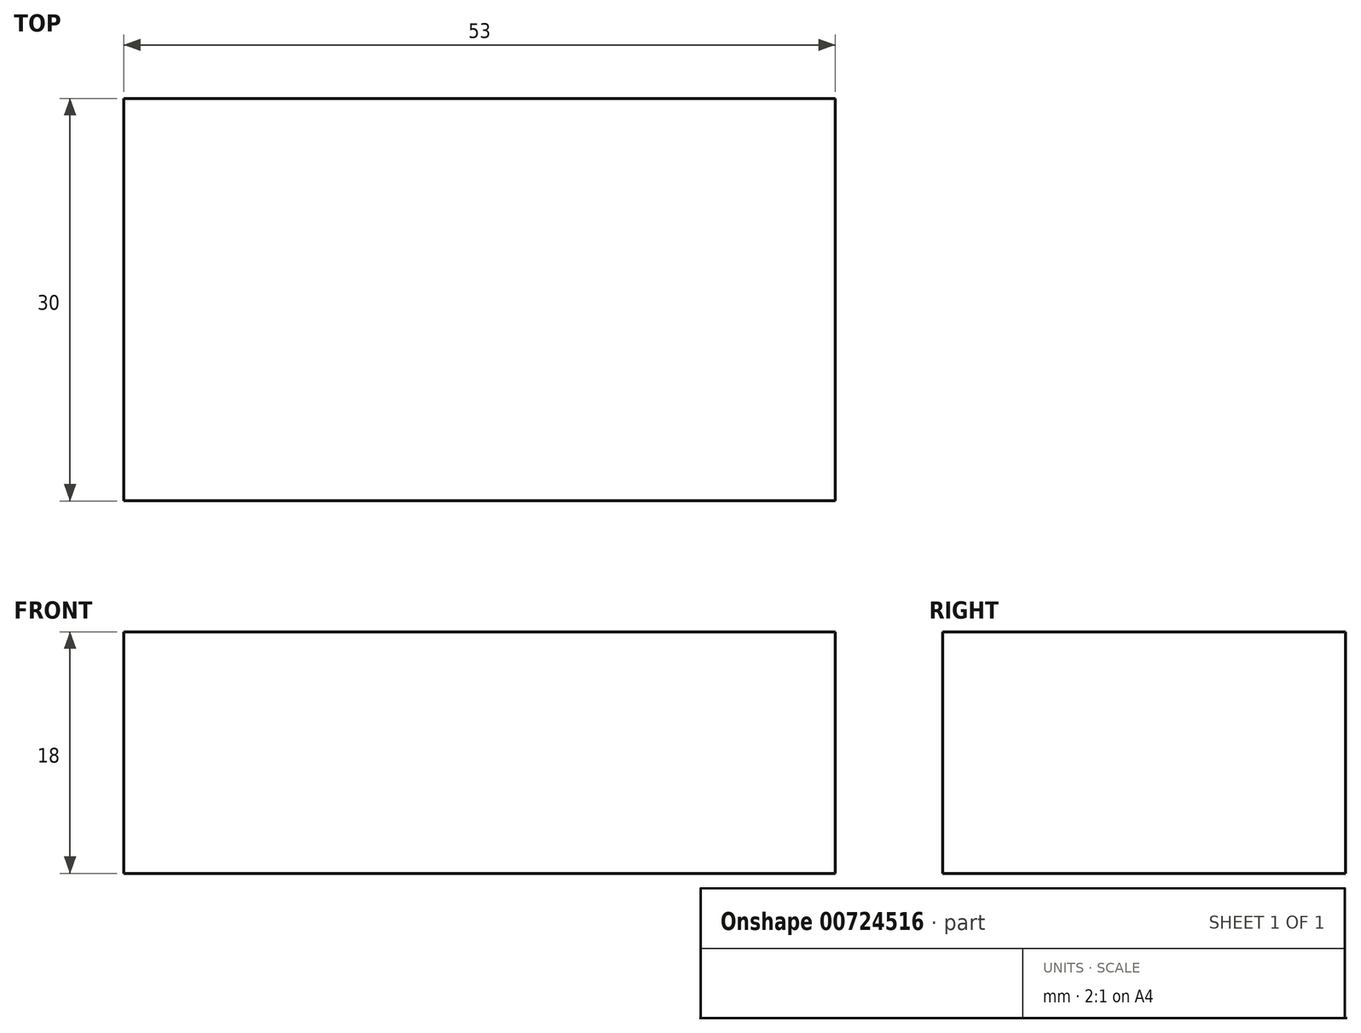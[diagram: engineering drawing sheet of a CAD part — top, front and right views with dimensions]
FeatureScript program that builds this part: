
annotation { "Feature Type Name" : "Feature", "Feature Type Description" : "" }
export const myFeature = defineFeature(function(context is Context, id is Id, definition is map)
    precondition{}
    {
        {
            var Q0;
            Q0=qCreatedBy(makeId("Top.planeOp"),FACE);
            var sketch = newSketch(context, id + "F0", { "sketchPlane" : qUnion([Q0])});
            skLineSegment(sketch, "E0.bottom", {"start": v(-23.42, 17.73) * mm, "end": v(29.58, 17.73) * mm});
            skLineSegment(sketch, "E0.top", {"start": v(-23.42, -12.27) * mm, "end": v(29.58, -12.27) * mm});
            skLineSegment(sketch, "E0.left", {"start": v(-23.42, 17.73) * mm, "end": v(-23.42, -12.27) * mm});
            skLineSegment(sketch, "E0.right", {"start": v(29.58, 17.73) * mm, "end": v(29.58, -12.27) * mm});
            skSolve(sketch);
        }
        {
            var Q0;
            Q0=makeQuery(id+"F0.imprint","IMPRINT",FACE,{"disambiguationData":[TD([[makeQuery(id+"F0.imprint","IMPRINT",EDGE,{"derivedFrom":sQuery(id+"F0.wireOp",EDGE,"E0.bottom")}),-1.0]])]});
            extrude(context, id + "F1", {"entities" : qUnion([Q0]), "endBound" : BoundingType.SYMMETRIC, "depth" : 18 * mm, "offsetDistance" : 25 * mm});
        }
    });
